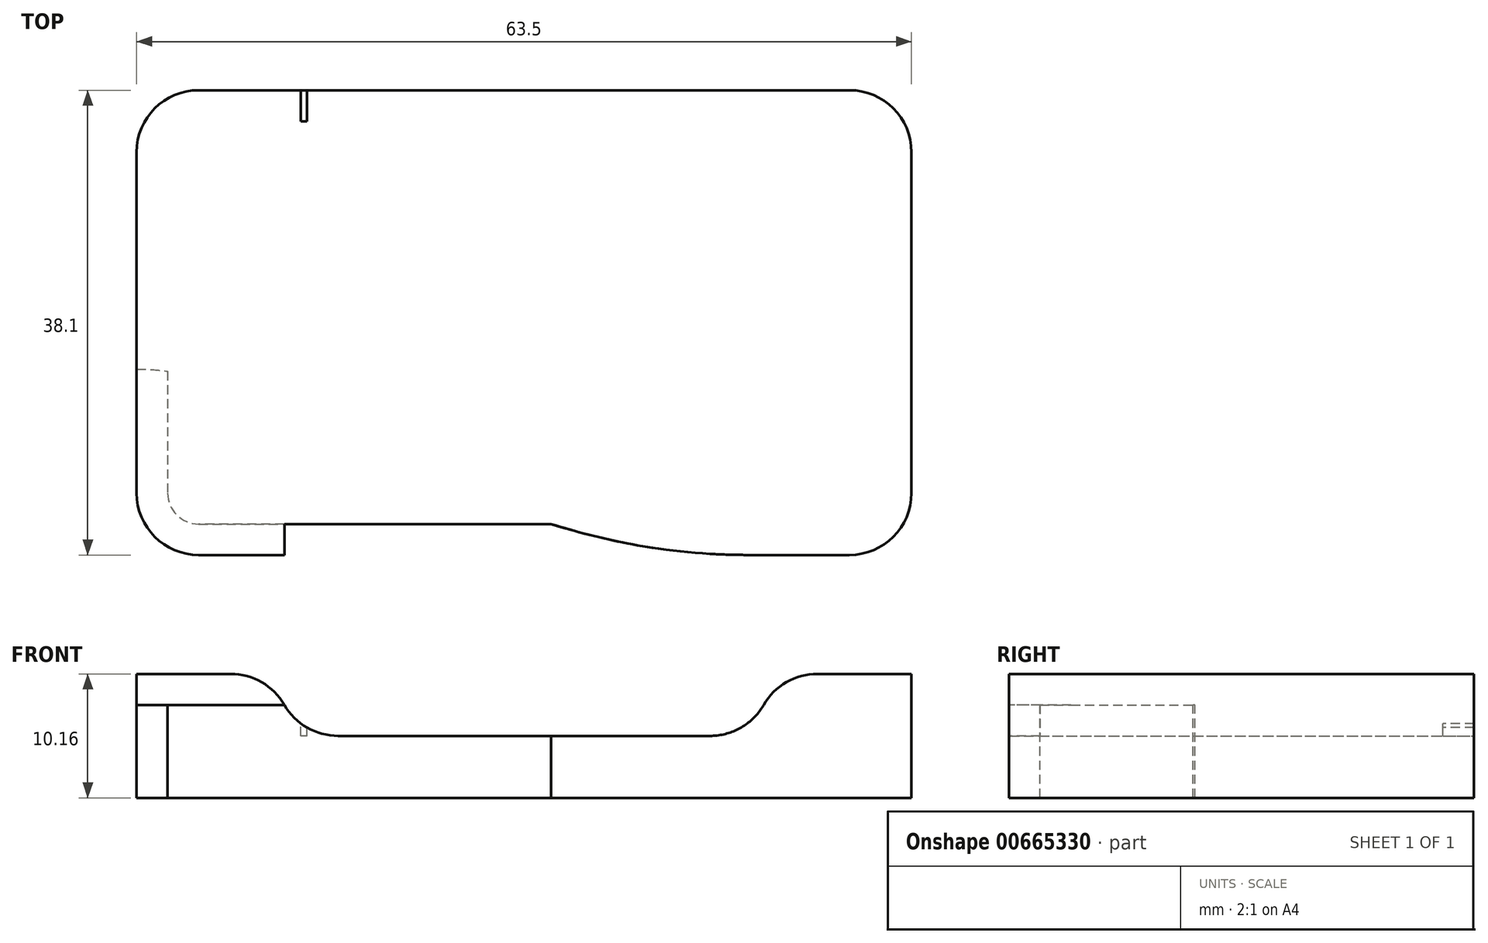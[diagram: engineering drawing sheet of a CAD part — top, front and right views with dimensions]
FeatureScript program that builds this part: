
annotation { "Feature Type Name" : "Feature", "Feature Type Description" : "" }
export const myFeature = defineFeature(function(context is Context, id is Id, definition is map)
    precondition{}
    {
        {
            var Q0;
            Q0=qCreatedBy(makeId("Top.planeOp"),FACE);
            var sketch = newSketch(context, id + "F0", { "sketchPlane" : qUnion([Q0])});
            skLineSegment(sketch, "E0.bottom", {"start": v(31.75, -19.05) * mm, "end": v(-31.75, -19.05) * mm});
            skLineSegment(sketch, "E0.top", {"start": v(31.75, 19.05) * mm, "end": v(-31.75, 19.05) * mm});
            skLineSegment(sketch, "E0.left", {"start": v(31.75, -19.05) * mm, "end": v(31.75, 19.05) * mm});
            skLineSegment(sketch, "E0.right", {"start": v(-31.75, -19.05) * mm, "end": v(-31.75, 19.05) * mm});
            skPoint(sketch, "E0.middle", {"position": v(0, 0) * mm});
            skSolve(sketch);
        }
        {
            var Q0;
            Q0=makeQuery(id+"F0.imprint","IMPRINT",FACE,{"disambiguationData":[TD([[makeQuery(id+"F0.imprint","IMPRINT",EDGE,{"derivedFrom":sQuery(id+"F0.wireOp",EDGE,"E0.bottom")}),-1.0]])]});
            extrude(context, id + "F1", {"entities" : qUnion([Q0]), "depth" : 10.16 * mm, "offsetDistance" : 25.4 * mm});
        }
        {
            var Q0;
            Q0=makeQuery(id+"F1.opExtrude","CAP_FACE",FACE,{"disambiguationData":[OSD([sQuery(id+"F0.wireOp",EDGE,"E0.bottom"),sQuery(id+"F0.wireOp",EDGE,"E0.top"),sQuery(id+"F0.wireOp",EDGE,"E0.left"),sQuery(id+"F0.wireOp",EDGE,"E0.right")])],"isStart":false});
            var sketch = newSketch(context, id + "F2", { "sketchPlane" : qUnion([Q0])});
            skLineSegment(sketch, "E1.bottom", {"start": v(20.32, -19.05) * mm, "end": v(-20.32, -19.05) * mm});
            skLineSegment(sketch, "E1.top", {"start": v(20.32, 19.05) * mm, "end": v(-20.32, 19.05) * mm});
            skLineSegment(sketch, "E1.left", {"start": v(20.32, -19.05) * mm, "end": v(20.32, 19.05) * mm});
            skLineSegment(sketch, "E1.right", {"start": v(-20.32, -19.05) * mm, "end": v(-20.32, 19.05) * mm});
            skPoint(sketch, "E1.middle", {"position": v(0, 0) * mm});
            skSolve(sketch);
        }
        {
            var Q0;
            Q0=makeQuery(id+"F2.imprint","IMPRINT",FACE,{"disambiguationData":[TD([[makeQuery(id+"F2.imprint","IMPRINT",EDGE,{"derivedFrom":sQuery(id+"F2.wireOp",EDGE,"E1.bottom")}),-1.0]])]});
            extrude(context, id + "F3", {"entities" : qUnion([Q0]), "operationType" : NewBodyOperationType.REMOVE, "oppositeDirection" : true, "depth" : 5.08 * mm, "offsetDistance" : 25.4 * mm});
        }
        {
            var Q0;
            Q0=makeQuery(id+"F1.opExtrude","SWEPT_EDGE",EDGE,{"disambiguationData":[OSD([sQuery(id+"F0.wireOp",EDGE,"E0.bottom"),sQuery(id+"F0.wireOp",EDGE,"E0.right")])]});
            var Q1;
            Q1=makeQuery(id+"F1.opExtrude","SWEPT_EDGE",EDGE,{"disambiguationData":[OSD([sQuery(id+"F0.wireOp",EDGE,"E0.top"),sQuery(id+"F0.wireOp",EDGE,"E0.right")])]});
            var Q2;
            Q2=makeQuery(id+"F1.opExtrude","SWEPT_EDGE",EDGE,{"disambiguationData":[OSD([sQuery(id+"F0.wireOp",EDGE,"E0.bottom"),sQuery(id+"F0.wireOp",EDGE,"E0.left")])]});
            var Q3;
            Q3=makeQuery(id+"F1.opExtrude","SWEPT_EDGE",EDGE,{"disambiguationData":[OSD([sQuery(id+"F0.wireOp",EDGE,"E0.top"),sQuery(id+"F0.wireOp",EDGE,"E0.left")])]});
            fillet(context, id + "F4", {"entities" : qUnion([Q0, Q1, Q2, Q3]), "radius" : 5.08 * mm, "tangentPropagation" : true, "allowEdgeOverflow" : false});
        }
        {
            var Q0;
            Q0=makeQuery(id+"F3.boolean.opBoolean","COPY",EDGE,{"derivedFrom":makeQuery(id+"F3.opExtrude","CAP_EDGE",EDGE,{"disambiguationData":[OSD([sQuery(id+"F2.wireOp",EDGE,"E1.right")])],"isStart":false})});
            var Q1;
            Q1=makeQuery(id+"F3.boolean.opBoolean","COPY",EDGE,{"derivedFrom":makeQuery(id+"F3.opExtrude","CAP_EDGE",EDGE,{"disambiguationData":[OSD([sQuery(id+"F2.wireOp",EDGE,"E1.left")])],"isStart":false})});
            fillet(context, id + "F5", {"entities" : qUnion([Q0, Q1]), "radius" : 5.08 * mm, "tangentPropagation" : true, "allowEdgeOverflow" : false});
        }
        {
            var Q0;
            {var subQ0=sQuery(id+"F0.wireOp",EDGE,"E0.bottom");var subQ1=sQuery(id+"F0.wireOp",EDGE,"E0.right");var subQ2=sQuery(id+"F0.wireOp",EDGE,"E0.top");var subQ3=sQuery(id+"F2.wireOp",EDGE,"E1.right");Q0=makeQuery(id+"F5.opFillet","BLEND_EDGE",EDGE,{"blendedFrom":[makeQuery(id+"F3.boolean.opBoolean","COPY",EDGE,{"derivedFrom":makeQuery(id+"F3.opExtrude","CAP_EDGE",EDGE,{"disambiguationData":[OSD([subQ3])],"isStart":false})}),makeQuery(id+"F3.boolean.opBoolean","SPLIT",FACE,{"disambiguationData":[TD([makeQuery(id+"F1.opExtrude","SWEPT_FACE",FACE,{"disambiguationData":[OSD([subQ1])]})])],"derivedFrom":makeQuery(id+"F1.opExtrude","CAP_FACE",FACE,{"disambiguationData":[OSD([subQ0,subQ2,sQuery(id+"F0.wireOp",EDGE,"E0.left"),subQ1])],"isStart":false})})],"blendedInto":[makeQuery(id+"F3.boolean.opBoolean","SPLIT",FACE,{"disambiguationData":[TD([makeQuery(id+"F1.opExtrude","SWEPT_FACE",FACE,{"disambiguationData":[OSD([subQ1])]})])],"derivedFrom":makeQuery(id+"F1.opExtrude","CAP_FACE",FACE,{"disambiguationData":[OSD([subQ0,subQ2,sQuery(id+"F0.wireOp",EDGE,"E0.left"),subQ1])],"isStart":false})})]});}
            var Q1;
            {var subQ0=sQuery(id+"F0.wireOp",EDGE,"E0.bottom");var subQ1=sQuery(id+"F0.wireOp",EDGE,"E0.top");var subQ2=sQuery(id+"F0.wireOp",EDGE,"E0.left");var subQ3=sQuery(id+"F2.wireOp",EDGE,"E1.left");Q1=makeQuery(id+"F5.opFillet","BLEND_EDGE",EDGE,{"blendedFrom":[makeQuery(id+"F3.boolean.opBoolean","COPY",EDGE,{"derivedFrom":makeQuery(id+"F3.opExtrude","CAP_EDGE",EDGE,{"disambiguationData":[OSD([subQ3])],"isStart":false})}),makeQuery(id+"F3.boolean.opBoolean","SPLIT",FACE,{"disambiguationData":[TD([makeQuery(id+"F1.opExtrude","SWEPT_FACE",FACE,{"disambiguationData":[OSD([subQ2])]})])],"derivedFrom":makeQuery(id+"F1.opExtrude","CAP_FACE",FACE,{"disambiguationData":[OSD([subQ0,subQ1,subQ2,sQuery(id+"F0.wireOp",EDGE,"E0.right")])],"isStart":false})})],"blendedInto":[makeQuery(id+"F3.boolean.opBoolean","SPLIT",FACE,{"disambiguationData":[TD([makeQuery(id+"F1.opExtrude","SWEPT_FACE",FACE,{"disambiguationData":[OSD([subQ2])]})])],"derivedFrom":makeQuery(id+"F1.opExtrude","CAP_FACE",FACE,{"disambiguationData":[OSD([subQ0,subQ1,subQ2,sQuery(id+"F0.wireOp",EDGE,"E0.right")])],"isStart":false})})]});}
            fillet(context, id + "F6", {"entities" : qUnion([Q0, Q1]), "radius" : 5.08 * mm, "tangentPropagation" : true, "allowEdgeOverflow" : false});
        }
        {
            var Q0;
            Q0=makeQuery(id+"F1.opExtrude","SWEPT_BODY",BODY,{"disambiguationData":[OSD([sQuery(id+"F0.wireOp",EDGE,"E0.bottom"),sQuery(id+"F0.wireOp",EDGE,"E0.top"),sQuery(id+"F0.wireOp",EDGE,"E0.left"),sQuery(id+"F0.wireOp",EDGE,"E0.right")])]});
            transform(context, id + "F7", {"entities" : qUnion([Q0]), "transformType" : TransformType.TRANSLATION_3D, "dx" : 0 * mm, "dy" : 0 * mm, "dz" : 0 * mm, "makeCopy" : true});
        }
        {
            var Q0;
            Q0=makeQuery(id+"F7.opPattern","COPY",BODY,{"derivedFrom":makeQuery(id+"F1.opExtrude","SWEPT_BODY",BODY,{"disambiguationData":[OSD([sQuery(id+"F0.wireOp",EDGE,"E0.bottom"),sQuery(id+"F0.wireOp",EDGE,"E0.top"),sQuery(id+"F0.wireOp",EDGE,"E0.left"),sQuery(id+"F0.wireOp",EDGE,"E0.right")])]}),"instanceName":"1"});
            deleteBodies(context, id + "F8", {"entities" : qUnion([Q0])});
        }
        {
            var Q0;
            Q0=makeQuery(id+"F1.opExtrude","CAP_FACE",FACE,{"disambiguationData":[OSD([sQuery(id+"F0.wireOp",EDGE,"E0.bottom"),sQuery(id+"F0.wireOp",EDGE,"E0.top"),sQuery(id+"F0.wireOp",EDGE,"E0.left"),sQuery(id+"F0.wireOp",EDGE,"E0.right")])],"isStart":true});
            var sketch = newSketch(context, id + "F9", { "sketchPlane" : qUnion([Q0])});
            skLineSegment(sketch, "E2.0", {"start": v(26.67, 19.05) * mm, "end": v(-26.67, 19.05) * mm});
            skArc(sketch, "E3.0", {"start": v(-26.67, 19.05) * mm, "mid": v(-30.26, 17.56) * mm, "end": v(-31.75, 13.97) * mm});
            skLineSegment(sketch, "E4.0", {"start": v(-31.75, 13.97) * mm, "end": v(-31.75, -13.97) * mm});
            skArc(sketch, "E5.0", {"start": v(-31.75, -13.97) * mm, "mid": v(-30.26, -17.56) * mm, "end": v(-26.67, -19.05) * mm});
            skLineSegment(sketch, "E6.0", {"start": v(26.67, -19.05) * mm, "end": v(-26.67, -19.05) * mm});
            skArc(sketch, "E7.0", {"start": v(26.67, -19.05) * mm, "mid": v(30.26, -17.56) * mm, "end": v(31.75, -13.97) * mm});
            skLineSegment(sketch, "E8.0", {"start": v(31.75, 13.97) * mm, "end": v(31.75, -13.97) * mm});
            skArc(sketch, "E9.0", {"start": v(31.75, 13.97) * mm, "mid": v(30.26, 17.56) * mm, "end": v(26.67, 19.05) * mm});
            skSolve(sketch);
        }
        {
            var Q0;
            Q0 = qSketchRegion(id + "F9", true);
            extrude(context, id + "F10", {"entities" : qUnion([Q0]), "oppositeDirection" : true, "depth" : 7.62 * mm, "offsetDistance" : 25.4 * mm});
        }
        {
            var Q0;
            Q0=makeQuery(id+"F10.opExtrude","CAP_EDGE",EDGE,{"disambiguationData":[OSD([sQuery(id+"F9.wireOp",EDGE,"E2.0")])],"isStart":false});
            var Q1;
            Q1=makeQuery(id+"F10.opExtrude","CAP_EDGE",EDGE,{"disambiguationData":[OSD([sQuery(id+"F9.wireOp",EDGE,"E2.0")])],"isStart":true});
            fillet(context, id + "F11", {"entities" : qUnion([Q0, Q1]), "radius" : 2.54 * mm, "tangentPropagation" : true, "allowEdgeOverflow" : false});
        }
        {
            var Q0;
            Q0=makeQuery(id+"F10.opExtrude","CAP_FACE",FACE,{"disambiguationData":[OSD([sQuery(id+"F9.wireOp",EDGE,"E2.0"),sQuery(id+"F9.wireOp",EDGE,"E3.0"),sQuery(id+"F9.wireOp",EDGE,"E4.0"),sQuery(id+"F9.wireOp",EDGE,"E5.0"),sQuery(id+"F9.wireOp",EDGE,"E6.0"),sQuery(id+"F9.wireOp",EDGE,"E7.0"),sQuery(id+"F9.wireOp",EDGE,"E8.0"),sQuery(id+"F9.wireOp",EDGE,"E9.0")])],"isStart":false});
            var sketch = newSketch(context, id + "F12", { "sketchPlane" : qUnion([Q0])});
            skLineSegment(sketch, "E10.bottom", {"start": v(17.78, -19.05) * mm, "end": v(-17.78, -19.05) * mm, "construction": true});
            skLineSegment(sketch, "E10.top", {"start": v(17.78, 19.05) * mm, "end": v(-17.78, 19.05) * mm, "construction": true});
            skLineSegment(sketch, "E10.left", {"start": v(17.78, -19.05) * mm, "end": v(17.78, 19.05) * mm});
            skLineSegment(sketch, "E10.right", {"start": v(-17.78, -19.05) * mm, "end": v(-17.78, 19.05) * mm});
            skPoint(sketch, "E10.middle", {"position": v(0, 0) * mm});
            skLineSegment(sketch, "E11.bottom", {"start": v(-17.78, 19.05) * mm, "end": v(-18.29, 19.05) * mm});
            skLineSegment(sketch, "E11.top", {"start": v(-17.78, -19.05) * mm, "end": v(-18.29, -19.05) * mm});
            skLineSegment(sketch, "E11.left", {"start": v(-17.78, 19.05) * mm, "end": v(-17.78, -19.05) * mm});
            skLineSegment(sketch, "E11.right", {"start": v(-18.29, 19.05) * mm, "end": v(-18.29, -19.05) * mm});
            skSolve(sketch);
        }
        {
            var Q0;
            {var subQ0=sQuery(id+"F12.wireOp",EDGE,"E11.left");var subQ1=sQuery(id+"F9.wireOp",EDGE,"E6.0");var subQ2=sQuery(id+"F9.wireOp",EDGE,"E2.0");var subQ3=makeQuery(id+"F10.opExtrude","CAP_FACE",FACE,{"disambiguationData":[OSD([subQ2,sQuery(id+"F9.wireOp",EDGE,"E3.0"),sQuery(id+"F9.wireOp",EDGE,"E4.0"),sQuery(id+"F9.wireOp",EDGE,"E5.0"),subQ1,sQuery(id+"F9.wireOp",EDGE,"E7.0"),sQuery(id+"F9.wireOp",EDGE,"E8.0"),sQuery(id+"F9.wireOp",EDGE,"E9.0")])],"isStart":false});var subQ4=makeQuery(id+"F11.opFillet","BLEND_EDGE",EDGE,{"blendedFrom":[makeQuery(id+"F10.opExtrude","CAP_EDGE",EDGE,{"disambiguationData":[OSD([subQ1])],"isStart":false}),subQ3],"blendedInto":[subQ3]});var subQ5=makeQuery(id+"F12.imprint","INTERSECT",VERTEX,{"derivedFrom":[subQ4,subQ0]});Q0=makeQuery(id+"F12.imprint","IMPRINT",FACE,{"disambiguationData":[TD([[makeQuery(id+"F12.imprint","IMPRINT",EDGE,{"disambiguationData":[TD([[subQ5,-1.0]])],"derivedFrom":subQ0}),-1.0]])]});}
            var Q1;
            {var subQ0=sQuery(id+"F12.wireOp",EDGE,"E11.bottom");Q1=makeQuery(id+"F12.imprint","IMPRINT",FACE,{"disambiguationData":[TD([[makeQuery(id+"F12.imprint","IMPRINT",EDGE,{"derivedFrom":subQ0}),1.0]])]});}
            var Q2;
            {var subQ0=sQuery(id+"F12.wireOp",EDGE,"E11.top");Q2=makeQuery(id+"F12.imprint","IMPRINT",FACE,{"disambiguationData":[TD([[makeQuery(id+"F12.imprint","IMPRINT",EDGE,{"derivedFrom":subQ0}),-1.0]])]});}
            extrude(context, id + "F13", {"entities" : qUnion([Q0, Q1, Q2]), "operationType" : NewBodyOperationType.REMOVE, "oppositeDirection" : true, "depth" : 2.54 * mm, "offsetDistance" : 25.4 * mm});
        }
        {
            var Q0;
            Q0=makeQuery(id+"F10.opExtrude","SWEPT_BODY",BODY,{"disambiguationData":[OSD([sQuery(id+"F9.wireOp",EDGE,"E2.0"),sQuery(id+"F9.wireOp",EDGE,"E3.0"),sQuery(id+"F9.wireOp",EDGE,"E4.0"),sQuery(id+"F9.wireOp",EDGE,"E5.0"),sQuery(id+"F9.wireOp",EDGE,"E6.0"),sQuery(id+"F9.wireOp",EDGE,"E7.0"),sQuery(id+"F9.wireOp",EDGE,"E8.0"),sQuery(id+"F9.wireOp",EDGE,"E9.0")])]});
            transform(context, id + "F14", {"entities" : qUnion([Q0]), "transformType" : TransformType.TRANSLATION_3D, "dx" : 0 * mm, "dy" : 0 * mm, "dz" : 0 * mm, "makeCopy" : true});
        }
        {
            var Q0;
            {var subQ0=sQuery(id+"F9.wireOp",EDGE,"E2.0");var subQ2=sQuery(id+"F12.wireOp",EDGE,"E11.left");var subQ3=makeQuery(id+"F13.opExtrude","SWEPT_FACE",FACE,{"disambiguationData":[OSD([subQ2])]});var subQ4=sQuery(id+"F9.wireOp",EDGE,"E6.0");var subQ6=sQuery(id+"F9.wireOp",EDGE,"E8.0");var subQ7=sQuery(id+"F9.wireOp",EDGE,"E7.0");var subQ8=sQuery(id+"F9.wireOp",EDGE,"E9.0");Q0=makeQuery(id+"F14.opPattern","COPY",FACE,{"derivedFrom":makeQuery(id+"FZbfRHft5HWekoC_2.1.F13.boolean.opBoolean","SPLIT",FACE,{"disambiguationData":[TD([makeQuery(id+"F13.boolean.opBoolean","COPY",FACE,{"derivedFrom":subQ3})])],"derivedFrom":makeQuery(id+"F13.boolean.opBoolean","SPLIT",FACE,{"disambiguationData":[TD([subQ3])],"derivedFrom":makeQuery(id+"F10.opExtrude","CAP_FACE",FACE,{"disambiguationData":[OSD([subQ0,sQuery(id+"F9.wireOp",EDGE,"E3.0"),sQuery(id+"F9.wireOp",EDGE,"E4.0"),sQuery(id+"F9.wireOp",EDGE,"E5.0"),subQ4,subQ7,subQ6,subQ8])],"isStart":false})})}),"instanceName":"1"});}
            var sketch = newSketch(context, id + "F15", { "sketchPlane" : qUnion([Q0])});
            skLineSegment(sketch, "E12.0", {"start": v(-31.75, -13.97) * mm, "end": v(-31.75, 13.97) * mm});
            skPoint(sketch, "E13.0", {"position": v(18.29, -19.05) * mm});
            skFitSpline(sketch, "E14", {"points": [v(-31.75, -3.81) * mm, v(18.29, -19.05) * mm], "startDerivative": vector(40.39, 0) * mm, "endDerivative": vector(68.58, 0) * mm});
            skPoint(sketch, "E15.0", {"position": v(-26.67, 19.05) * mm});
            skLineSegment(sketch, "E16", {"start": v(-26.67, 19.05) * mm, "end": v(-39.37, 19.05) * mm});
            skLineSegment(sketch, "E17", {"start": v(-31.75, -3.81) * mm, "end": v(-31.75, -19.05) * mm});
            skLineSegment(sketch, "E18", {"start": v(-31.75, -19.05) * mm, "end": v(18.29, -19.05) * mm});
            skSolve(sketch);
        }
        {
            var Q0;
            {var subQ0=sQuery(id+"F15.wireOp",EDGE,"E18");Q0=makeQuery(id+"F15.imprint","IMPRINT",FACE,{"disambiguationData":[TD([[makeQuery(id+"F15.imprint","IMPRINT",EDGE,{"derivedFrom":subQ0}),1.0]])]});}
            var Q1;
            {var subQ0=sQuery(id+"F15.wireOp",EDGE,"E14");var subQ1=sQuery(id+"F12.wireOp",EDGE,"E11.left");var subQ2=makeQuery(id+"F14.opPattern","COPY",EDGE,{"derivedFrom":makeQuery(id+"F13.boolean.opBoolean","COPY",EDGE,{"derivedFrom":makeQuery(id+"F13.opExtrude","CAP_EDGE",EDGE,{"disambiguationData":[OSD([subQ1])],"isStart":true})}),"instanceName":"1"});var subQ3=makeQuery(id+"F15.imprint","INTERSECT",VERTEX,{"derivedFrom":[subQ2,subQ0]});Q1=makeQuery(id+"F15.imprint","IMPRINT",FACE,{"disambiguationData":[TD([[makeQuery(id+"F15.imprint","IMPRINT",EDGE,{"disambiguationData":[TD([[subQ3,-1.0]])],"derivedFrom":subQ0}),-1.0]])]});}
            extrude(context, id + "F16", {"entities" : qUnion([Q0, Q1]), "operationType" : NewBodyOperationType.REMOVE, "endBound" : BoundingType.THROUGH_ALL, "oppositeDirection" : true, "depth" : 25.4 * mm, "offsetDistance" : 25.4 * mm});
        }
        {
            var Q0;
            Q0=makeQuery(id+"F14.opPattern","COPY",BODY,{"derivedFrom":makeQuery(id+"F10.opExtrude","SWEPT_BODY",BODY,{"disambiguationData":[OSD([sQuery(id+"F9.wireOp",EDGE,"E2.0"),sQuery(id+"F9.wireOp",EDGE,"E3.0"),sQuery(id+"F9.wireOp",EDGE,"E4.0"),sQuery(id+"F9.wireOp",EDGE,"E5.0"),sQuery(id+"F9.wireOp",EDGE,"E6.0"),sQuery(id+"F9.wireOp",EDGE,"E7.0"),sQuery(id+"F9.wireOp",EDGE,"E8.0"),sQuery(id+"F9.wireOp",EDGE,"E9.0")])]}),"instanceName":"1"});
            deleteBodies(context, id + "F17", {"entities" : qUnion([Q0])});
        }
        {
            var Q0;
            Q0=makeQuery(id+"F10.opExtrude","SWEPT_BODY",BODY,{"disambiguationData":[OSD([sQuery(id+"F9.wireOp",EDGE,"E2.0"),sQuery(id+"F9.wireOp",EDGE,"E3.0"),sQuery(id+"F9.wireOp",EDGE,"E4.0"),sQuery(id+"F9.wireOp",EDGE,"E5.0"),sQuery(id+"F9.wireOp",EDGE,"E6.0"),sQuery(id+"F9.wireOp",EDGE,"E7.0"),sQuery(id+"F9.wireOp",EDGE,"E8.0"),sQuery(id+"F9.wireOp",EDGE,"E9.0")])]});
            deleteBodies(context, id + "F18", {"entities" : qUnion([Q0])});
        }
    });
